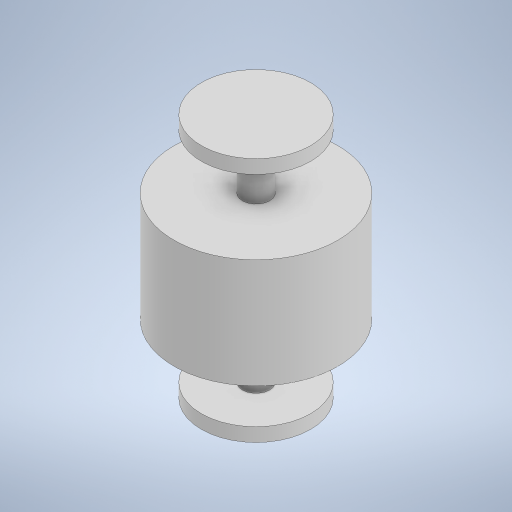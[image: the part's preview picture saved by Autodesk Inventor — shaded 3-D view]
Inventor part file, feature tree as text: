
AUTODESK INVENTOR PART (.ipt)
format: ipt  version: 2023 (Build 270158030, 158C)  size: 240,128 bytes
history: native  units: in
note: dims shown in document units (in); Inventor stores cm internally (conversion verified against a paired STEP export)
features: extrude x5, sketch x4
ambient origin geometry x8: Origin, YZ Plane, XZ Plane, XY Plane, X Axis, Y Axis, Z Axis, Center Point
bodies: Solid1 (feature_tree)
feature tree (9):
  extrude  "Extrusion1"  Depth=1.0in TaperAngle=0.0deg
  sketch  "Sketch2"  dims[d3=0.25in d4=0.5in d5=0.0in]
  extrude  "Extrusion2"  Depth=0.5in TaperAngle=0.0deg
  extrude  "Extrusion3"  Depth=1.0in
  extrude  "Extrusion4"  Depth=1.0in
  extrude  "Extrusion5"  Depth=0.125in TaperAngle=0.0deg
  sketch  "Sketch1"  dims[d0=1.5in d1=1.0in d2=0.0in]
  sketch  "Sketch3"  dims[d6=1.5in d7=0.0in d8=1.0in]
  sketch  "Sketch4"  dims[d9=0.125in d10=0.0in d11=1.0in d12=0.125in d13=0.0in]
